# Revit family: Go mirror cabinets 600 800
name_source: partatom
category: Furniture
units: mm (PartAtom-declared; Revit-internal decimal feet)

## family parameters
Always vertical = Yes
Cut with Voids When Loaded = No
OmniClass Number = 23.40.20.00
OmniClass Title = General Furniture and Specialties
Room Calculation Point = No
Shared = No
Work Plane-Based = No

## types (4) — shared parameters
Body material = MDF/HDF/Chripboard moisture restistant E1 and FSC certified.
Depth cabinet = 145 mm  [stored 0.475722 ft]
Glass doors = Mirror glass
Manufacturer = Hafa Bathroom Group AB
Model = Go mirror cabinets
URL = www.hafa.se

## per-type parameters (varying)
| type | Article number | Cabinet body | GTIN | Width cabinet |
| Go mirror cabinet 600 white matt | 1580220 | NCS S 0300-N 20% gloss | 7330027103617 | 600 mm |
| Go mirror cabinet 800 white matt | 1580230 | NCS S 0300-N 20% gloss | 7330027103631 | 800 mm  [stored 2.62467 ft] |
| Go mirror cabinet 800 black matt | 1580231 | NCS S 9000-N 10% gloss | 7330027103648 | 800 mm  [stored 2.62467 ft] |
| Go mirror cabinet 600 black matt | 1580221 | NCS S 9000-N 10% gloss | 7330027103624 | 600 mm |

note: [stored X ft] marks values corroborated as IEEE doubles in the binary element streams (Revit-internal decimal feet)

## geometry (parser evidence)
native form markers: Sweep x2
no freeform markers — native parametric forms only
